# Revit family: Тренажер Кинезис Kinesis одномодульный Technogym
name_source: partatom
category: Оборудование
revit_build: Autodesk Revit 2017 (Build: 20170419_0315(x64)
units: mm (PartAtom-declared; Revit-internal decimal feet)

## family parameters
Всегда вертикально = Да
На основе рабочей плоскости = Нет
Общий = Нет
При загрузке вырезать с полостями = Нет
Размер круглого соединителя = Использовать диаметр
Тип детали = Нормальный
Точка расчета площади = Нет

## types (2) — shared parameters
Глубина = 1802 мм
Группа модели = ТХ
Единицы = шт.
Завод = Technogym
Ширина = 1360 мм

## per-type parameters (varying)
| type | Высота | Изготовитель | Код оборудования | Масса | Наименование | Обозначение |
| Многофункциональный тренажер Кинезис одномодульный | 2120 мм | Severin |  | 365 | Многофункциональный тренажер Кинезис одномодульный, габариты (ВГШ): 2120х1802х1360 | ML14 |
| 1640х1405х2120 | 1800 мм | Ant | ML14 | 365 кг. | Многофункциональный тренажер Кинезис Одномодульный | - |

## geometry (parser evidence)
native form markers: Blend x2
no freeform markers — native parametric forms only
